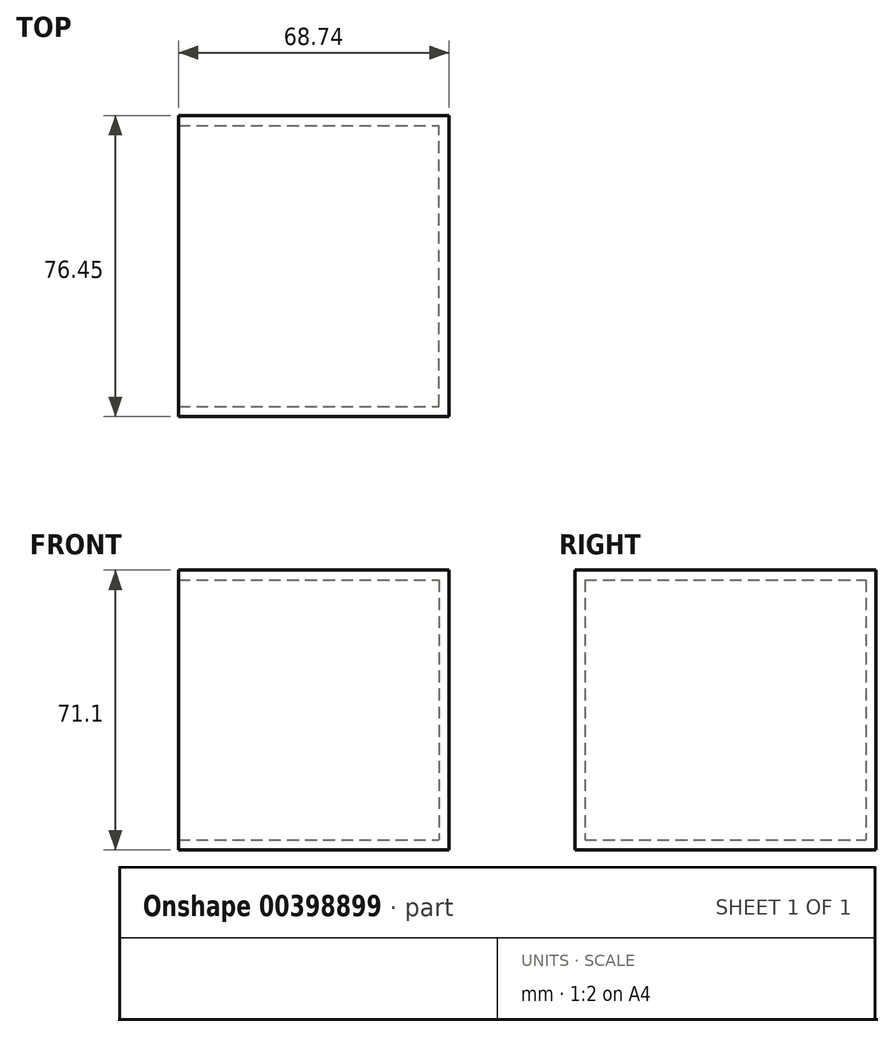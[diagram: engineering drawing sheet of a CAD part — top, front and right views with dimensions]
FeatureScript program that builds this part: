
annotation { "Feature Type Name" : "Feature", "Feature Type Description" : "" }
export const myFeature = defineFeature(function(context is Context, id is Id, definition is map)
    precondition{}
    {
        {
            var Q0;
            Q0=qCreatedBy(makeId("Front.planeOp"),FACE);
            var sketch = newSketch(context, id + "F0", { "sketchPlane" : qUnion([Q0])});
            skLineSegment(sketch, "E0.bottom", {"start": v(-27.85, 11.7) * mm, "end": v(40.89, 11.7) * mm});
            skLineSegment(sketch, "E0.top", {"start": v(-27.85, -59.4) * mm, "end": v(40.89, -59.4) * mm});
            skLineSegment(sketch, "E0.left", {"start": v(-27.85, 11.7) * mm, "end": v(-27.85, -59.4) * mm});
            skLineSegment(sketch, "E0.right", {"start": v(40.89, 11.7) * mm, "end": v(40.89, -59.4) * mm});
            skSolve(sketch);
        }
        {
            var Q0;
            Q0 = qSketchRegion(id + "F0", true);
            extrude(context, id + "F1", {"entities" : qUnion([Q0]), "depth" : 76.45 * mm});
        }
        {
            var Q0;
            Q0=makeQuery(id+"F1.opExtrude","SWEPT_FACE",FACE,{"disambiguationData":[OSD([sQuery(id+"F0.wireOp",EDGE,"E0.left")])]});
            shell(context, id + "F2", {"entities" : qUnion([Q0]), "thickness" : 2.54 * mm});
        }
    });
